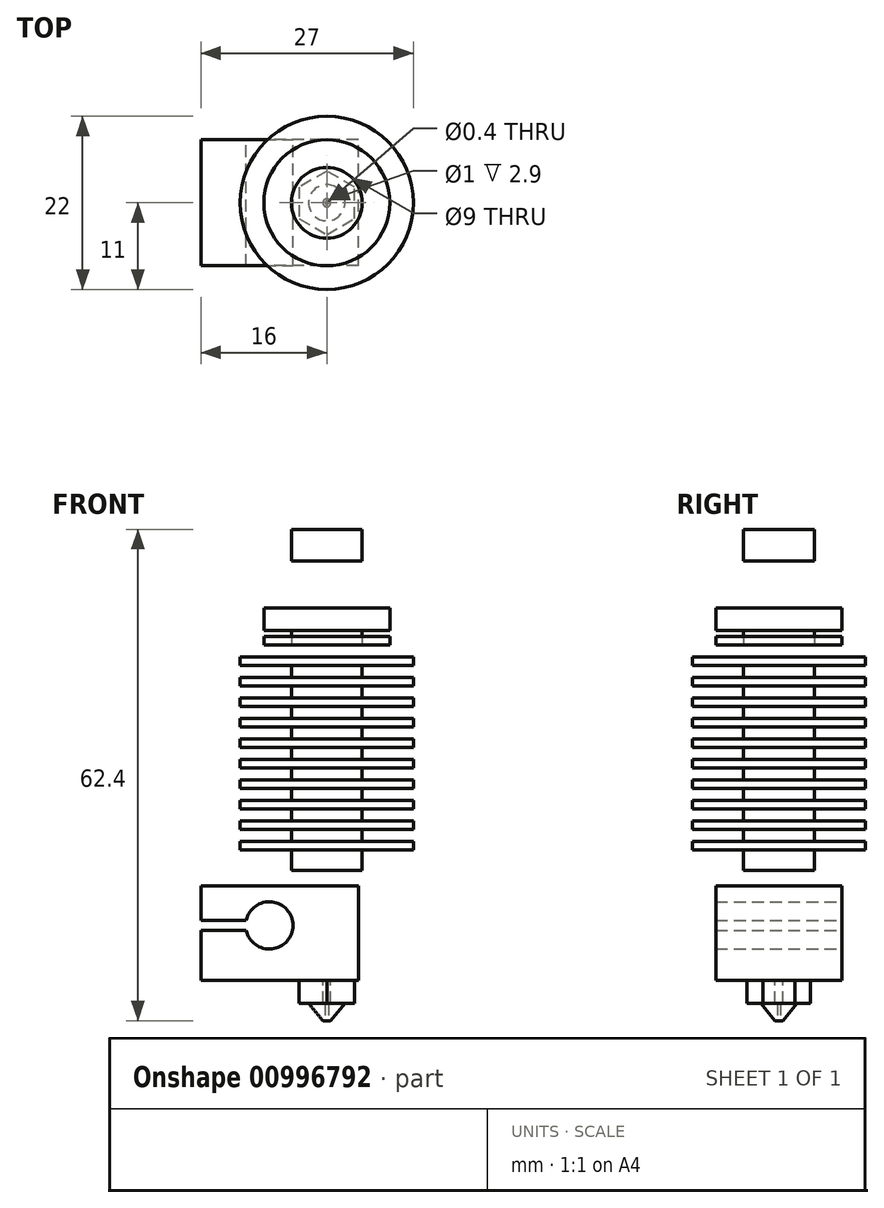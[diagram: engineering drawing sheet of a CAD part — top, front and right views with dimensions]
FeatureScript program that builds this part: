
annotation { "Feature Type Name" : "Feature", "Feature Type Description" : "" }
export const myFeature = defineFeature(function(context is Context, id is Id, definition is map)
    precondition{}
    {
        {
            var Q0;
            Q0=qCreatedBy(makeId("Front.planeOp"),FACE);
            var sketch = newSketch(context, id + "F0", { "sketchPlane" : qUnion([Q0])});
            skLineSegment(sketch, "E0.bottom", {"start": v(0, 0) * mm, "end": v(-11, 0) * mm});
            skLineSegment(sketch, "E0.top", {"start": v(0, 1.1) * mm, "end": v(-11, 1.1) * mm});
            skLineSegment(sketch, "E0.left", {"start": v(0, 0) * mm, "end": v(0, 1.1) * mm});
            skLineSegment(sketch, "E0.right", {"start": v(-11, 0) * mm, "end": v(-11, 1.1) * mm});
            skLineSegment(sketch, "E1.0.1.0", {"start": v(0, 3.7) * mm, "end": v(-11, 3.7) * mm});
            skLineSegment(sketch, "E1.0.1.1", {"start": v(-11, 2.6) * mm, "end": v(-11, 3.7) * mm});
            skLineSegment(sketch, "E1.0.1.2", {"start": v(0, 2.6) * mm, "end": v(-11, 2.6) * mm});
            skLineSegment(sketch, "E1.0.1.3", {"start": v(0, 2.6) * mm, "end": v(0, 3.7) * mm});
            skLineSegment(sketch, "E1.0.2.0", {"start": v(0, 6.3) * mm, "end": v(-11, 6.3) * mm});
            skLineSegment(sketch, "E1.0.2.1", {"start": v(-11, 5.2) * mm, "end": v(-11, 6.3) * mm});
            skLineSegment(sketch, "E1.0.2.2", {"start": v(0, 5.2) * mm, "end": v(-11, 5.2) * mm});
            skLineSegment(sketch, "E1.0.2.3", {"start": v(0, 5.2) * mm, "end": v(0, 6.3) * mm});
            skLineSegment(sketch, "E1.0.3.0", {"start": v(0, 8.9) * mm, "end": v(-11, 8.9) * mm});
            skLineSegment(sketch, "E1.0.3.1", {"start": v(-11, 7.8) * mm, "end": v(-11, 8.9) * mm});
            skLineSegment(sketch, "E1.0.3.2", {"start": v(0, 7.8) * mm, "end": v(-11, 7.8) * mm});
            skLineSegment(sketch, "E1.0.3.3", {"start": v(0, 7.8) * mm, "end": v(0, 8.9) * mm});
            skLineSegment(sketch, "E1.0.4.0", {"start": v(0, 11.5) * mm, "end": v(-11, 11.5) * mm});
            skLineSegment(sketch, "E1.0.4.1", {"start": v(-11, 10.4) * mm, "end": v(-11, 11.5) * mm});
            skLineSegment(sketch, "E1.0.4.2", {"start": v(0, 10.4) * mm, "end": v(-11, 10.4) * mm});
            skLineSegment(sketch, "E1.0.4.3", {"start": v(0, 10.4) * mm, "end": v(0, 11.5) * mm});
            skLineSegment(sketch, "E1.0.5.0", {"start": v(0, 14.1) * mm, "end": v(-11, 14.1) * mm});
            skLineSegment(sketch, "E1.0.5.1", {"start": v(-11, 13) * mm, "end": v(-11, 14.1) * mm});
            skLineSegment(sketch, "E1.0.5.2", {"start": v(0, 13) * mm, "end": v(-11, 13) * mm});
            skLineSegment(sketch, "E1.0.5.3", {"start": v(0, 13) * mm, "end": v(0, 14.1) * mm});
            skLineSegment(sketch, "E1.0.6.0", {"start": v(0, 16.7) * mm, "end": v(-11, 16.7) * mm});
            skLineSegment(sketch, "E1.0.6.1", {"start": v(-11, 15.6) * mm, "end": v(-11, 16.7) * mm});
            skLineSegment(sketch, "E1.0.6.2", {"start": v(0, 15.6) * mm, "end": v(-11, 15.6) * mm});
            skLineSegment(sketch, "E1.0.6.3", {"start": v(0, 15.6) * mm, "end": v(0, 16.7) * mm});
            skLineSegment(sketch, "E1.0.7.0", {"start": v(0, 19.3) * mm, "end": v(-11, 19.3) * mm});
            skLineSegment(sketch, "E1.0.7.1", {"start": v(-11, 18.2) * mm, "end": v(-11, 19.3) * mm});
            skLineSegment(sketch, "E1.0.7.2", {"start": v(0, 18.2) * mm, "end": v(-11, 18.2) * mm});
            skLineSegment(sketch, "E1.0.7.3", {"start": v(0, 18.2) * mm, "end": v(0, 19.3) * mm});
            skLineSegment(sketch, "E1.0.8.0", {"start": v(0, 21.9) * mm, "end": v(-11, 21.9) * mm});
            skLineSegment(sketch, "E1.0.8.1", {"start": v(-11, 20.8) * mm, "end": v(-11, 21.9) * mm});
            skLineSegment(sketch, "E1.0.8.2", {"start": v(0, 20.8) * mm, "end": v(-11, 20.8) * mm});
            skLineSegment(sketch, "E1.0.8.3", {"start": v(0, 20.8) * mm, "end": v(0, 21.9) * mm});
            skLineSegment(sketch, "E1.0.9.0", {"start": v(0, 24.5) * mm, "end": v(-11, 24.5) * mm});
            skLineSegment(sketch, "E1.0.9.1", {"start": v(-11, 23.4) * mm, "end": v(-11, 24.5) * mm});
            skLineSegment(sketch, "E1.0.9.2", {"start": v(0, 23.4) * mm, "end": v(-11, 23.4) * mm});
            skLineSegment(sketch, "E1.0.9.3", {"start": v(0, 23.4) * mm, "end": v(0, 24.5) * mm});
            skLineSegment(sketch, "E1.0.10.0", {"start": v(0, 27.1) * mm, "end": v(-11, 27.1) * mm});
            skLineSegment(sketch, "E1.0.10.1", {"start": v(-11, 26) * mm, "end": v(-11, 27.1) * mm});
            skLineSegment(sketch, "E1.0.10.2", {"start": v(0, 26) * mm, "end": v(-11, 26) * mm});
            skLineSegment(sketch, "E1.0.10.3", {"start": v(0, 26) * mm, "end": v(0, 27.1) * mm});
            skLineSegment(sketch, "E1.direction1", {"start": v(-11, 0) * mm, "end": v(14, 0) * mm, "construction": true});
            skLineSegment(sketch, "E1.direction2", {"start": v(-11, 0) * mm, "end": v(-11, 2.6) * mm, "construction": true});
            skLineSegment(sketch, "E2.bottom", {"start": v(0, 0) * mm, "end": v(-4.5, 0) * mm});
            skLineSegment(sketch, "E2.top", {"start": v(0, 30.5) * mm, "end": v(-4.5, 30.5) * mm});
            skLineSegment(sketch, "E2.left", {"start": v(0, 0) * mm, "end": v(0, 30.5) * mm});
            skLineSegment(sketch, "E2.right", {"start": v(-4.5, 0) * mm, "end": v(-4.5, 30.5) * mm});
            skLineSegment(sketch, "E3", {"start": v(0, 27.1) * mm, "end": v(0, 28.6) * mm});
            skLineSegment(sketch, "E4.bottom", {"start": v(0, 28.6) * mm, "end": v(-8, 28.6) * mm});
            skLineSegment(sketch, "E4.top", {"start": v(0, 29.7) * mm, "end": v(-8, 29.7) * mm});
            skLineSegment(sketch, "E4.left", {"start": v(0, 28.6) * mm, "end": v(0, 29.7) * mm});
            skLineSegment(sketch, "E4.right", {"start": v(-8, 28.6) * mm, "end": v(-8, 29.7) * mm});
            skLineSegment(sketch, "E5.bottom", {"start": v(0, 30.5) * mm, "end": v(-8, 30.5) * mm});
            skLineSegment(sketch, "E5.top", {"start": v(0, 33.3) * mm, "end": v(-8, 33.3) * mm});
            skLineSegment(sketch, "E5.left", {"start": v(0, 30.5) * mm, "end": v(0, 33.3) * mm});
            skLineSegment(sketch, "E5.right", {"start": v(-8, 30.5) * mm, "end": v(-8, 33.3) * mm});
            skLineSegment(sketch, "E6.bottom", {"start": v(0, 33.3) * mm, "end": v(-6, 33.3) * mm});
            skLineSegment(sketch, "E6.top", {"start": v(0, 39.3) * mm, "end": v(-6, 39.3) * mm});
            skLineSegment(sketch, "E6.left", {"start": v(0, 33.3) * mm, "end": v(0, 39.3) * mm});
            skLineSegment(sketch, "E6.right", {"start": v(-6, 33.3) * mm, "end": v(-6, 39.3) * mm});
            skLineSegment(sketch, "E7.bottom", {"start": v(0, 39.3) * mm, "end": v(-8, 39.3) * mm});
            skLineSegment(sketch, "E7.top", {"start": v(0, 43.3) * mm, "end": v(-8, 43.3) * mm});
            skLineSegment(sketch, "E7.left", {"start": v(0, 39.3) * mm, "end": v(0, 43.3) * mm});
            skLineSegment(sketch, "E7.right", {"start": v(-8, 39.3) * mm, "end": v(-8, 43.3) * mm});
            skLineSegment(sketch, "E8.bottom", {"start": v(0, 33.3) * mm, "end": v(-4.5, 33.3) * mm});
            skLineSegment(sketch, "E8.top", {"start": v(0, 43.3) * mm, "end": v(-4.5, 43.3) * mm});
            skLineSegment(sketch, "E8.left", {"start": v(0, 33.3) * mm, "end": v(0, 43.3) * mm});
            skLineSegment(sketch, "E8.right", {"start": v(-4.5, 33.3) * mm, "end": v(-4.5, 43.3) * mm});
            skLineSegment(sketch, "E9.bottom", {"start": v(0, 0) * mm, "end": v(-4.15, 0) * mm});
            skLineSegment(sketch, "E9.top", {"start": v(0, -16.9) * mm, "end": v(-4.15, -16.9) * mm});
            skLineSegment(sketch, "E9.left", {"start": v(0, 0) * mm, "end": v(0, -16.9) * mm});
            skLineSegment(sketch, "E9.right", {"start": v(-4.15, 0) * mm, "end": v(-4.15, -16.9) * mm});
            skLineSegment(sketch, "E10", {"start": v(0, 0) * mm, "end": v(0, -2) * mm});
            skLineSegment(sketch, "E11", {"start": v(0, -2) * mm, "end": v(4, -2) * mm});
            skLineSegment(sketch, "E12.bottom", {"start": v(4, -2) * mm, "end": v(-16, -2) * mm});
            skLineSegment(sketch, "E12.top", {"start": v(4, -14) * mm, "end": v(-16, -14) * mm});
            skLineSegment(sketch, "E12.left", {"start": v(4, -2) * mm, "end": v(4, -14) * mm});
            skLineSegment(sketch, "E12.right", {"start": v(-16, -2) * mm, "end": v(-16, -14) * mm});
            skLineSegment(sketch, "E13.bottom", {"start": v(0, -16.9) * mm, "end": v(-0.2, -16.9) * mm});
            skLineSegment(sketch, "E13.top", {"start": v(0, -19.1) * mm, "end": v(-0.2, -19.1) * mm});
            skLineSegment(sketch, "E13.left", {"start": v(0, -16.9) * mm, "end": v(0, -19.1) * mm});
            skLineSegment(sketch, "E13.right", {"start": v(-0.2, -16.9) * mm, "end": v(-0.2, -19.1) * mm});
            skLineSegment(sketch, "E14", {"start": v(-0.2, -19.1) * mm, "end": v(-0.5, -19.1) * mm});
            skLineSegment(sketch, "E15", {"start": v(-0.2, -16.9) * mm, "end": v(-2.3, -16.9) * mm});
            skLineSegment(sketch, "E16", {"start": v(-2.3, -16.9) * mm, "end": v(-0.5, -19.1) * mm});
            skLineSegment(sketch, "E17", {"start": v(4, -14) * mm, "end": v(4, -7) * mm});
            skLineSegment(sketch, "E18", {"start": v(4, -7) * mm, "end": v(-7.3, -7) * mm, "construction": true});
            skCircle(sketch, "E19", {"center": v(-7.3, -7) * mm, "radius": 3 * mm});
            skLineSegment(sketch, "E20", {"start": v(-7.3, -7) * mm, "end": v(-7.3, -6.35) * mm, "construction": true});
            skLineSegment(sketch, "E21", {"start": v(-7.3, -7) * mm, "end": v(-7.3, -7.65) * mm, "construction": true});
            skLineSegment(sketch, "E22", {"start": v(-7.3, -7.65) * mm, "end": v(-16, -7.65) * mm});
            skLineSegment(sketch, "E23", {"start": v(-7.3, -6.35) * mm, "end": v(-16, -6.35) * mm});
            skLineSegment(sketch, "E24", {"start": v(-2.3, -16.9) * mm, "end": v(-2.3, 0) * mm});
            skSolve(sketch);
        }
        {
            var Q0;
            Q0=makeQuery(id+"F0.imprint","IMPRINT",FACE,{"disambiguationData":[TD([[makeQuery(id+"F0.imprint","IMPRINT",EDGE,{"derivedFrom":sQuery(id+"F0.wireOp",EDGE,"E13.right")}),-1.0]])]});
            var Q1;
            {var subQ0=sQuery(id+"F0.wireOp",EDGE,"E13.bottom");Q1=makeQuery(id+"F0.imprint","IMPRINT",FACE,{"disambiguationData":[TD([[makeQuery(id+"F0.imprint","IMPRINT",EDGE,{"derivedFrom":subQ0}),-1.0]])]});}
            var Q2;
            {var subQ1=sQuery(id+"F0.wireOp",EDGE,"E2.bottom");Q2=makeQuery(id+"F0.imprint","IMPRINT",FACE,{"disambiguationData":[TD([[makeQuery(id+"F0.imprint","IMPRINT",EDGE,{"derivedFrom":subQ1}),-1.0]])]});}
            var Q3;
            {var subQ0=sQuery(id+"F0.wireOp",EDGE,"E0.bottom");Q3=makeQuery(id+"F0.imprint","IMPRINT",FACE,{"disambiguationData":[TD([[makeQuery(id+"F0.imprint","IMPRINT",EDGE,{"derivedFrom":subQ0}),-1.0]])]});}
            var Q4;
            {var subQ0=sQuery(id+"F0.wireOp",EDGE,"E2.left");var subQ1=sQuery(id+"F0.wireOp",EDGE,"E0.top");var subQ2=makeQuery(id+"F0.imprint","INTERSECT",VERTEX,{"derivedFrom":[subQ1,subQ0]});Q4=makeQuery(id+"F0.imprint","IMPRINT",FACE,{"disambiguationData":[TD([[makeQuery(id+"F0.imprint","IMPRINT",EDGE,{"disambiguationData":[TD([[subQ2,-1.0]])],"derivedFrom":subQ1}),-1.0]])]});}
            var Q5;
            {var subQ0=sQuery(id+"F0.wireOp",EDGE,"E2.left");var subQ1=sQuery(id+"F0.wireOp",EDGE,"E1.0.1.0");var subQ2=makeQuery(id+"F0.imprint","INTERSECT",VERTEX,{"derivedFrom":[subQ1,subQ0]});Q5=makeQuery(id+"F0.imprint","IMPRINT",FACE,{"disambiguationData":[TD([[makeQuery(id+"F0.imprint","IMPRINT",EDGE,{"disambiguationData":[TD([[subQ2,-1.0]])],"derivedFrom":subQ1}),1.0]])]});}
            var Q6;
            {var subQ0=sQuery(id+"F0.wireOp",EDGE,"E1.0.1.1");Q6=makeQuery(id+"F0.imprint","IMPRINT",FACE,{"disambiguationData":[TD([[makeQuery(id+"F0.imprint","IMPRINT",EDGE,{"derivedFrom":subQ0}),-1.0]])]});}
            var Q7;
            {var subQ0=sQuery(id+"F0.wireOp",EDGE,"E2.left");var subQ1=sQuery(id+"F0.wireOp",EDGE,"E1.0.1.0");var subQ2=makeQuery(id+"F0.imprint","INTERSECT",VERTEX,{"derivedFrom":[subQ1,subQ0]});Q7=makeQuery(id+"F0.imprint","IMPRINT",FACE,{"disambiguationData":[TD([[makeQuery(id+"F0.imprint","IMPRINT",EDGE,{"disambiguationData":[TD([[subQ2,-1.0]])],"derivedFrom":subQ1}),-1.0]])]});}
            var Q8;
            {var subQ0=sQuery(id+"F0.wireOp",EDGE,"E2.left");var subQ1=sQuery(id+"F0.wireOp",EDGE,"E1.0.2.0");var subQ2=makeQuery(id+"F0.imprint","INTERSECT",VERTEX,{"derivedFrom":[subQ1,subQ0]});Q8=makeQuery(id+"F0.imprint","IMPRINT",FACE,{"disambiguationData":[TD([[makeQuery(id+"F0.imprint","IMPRINT",EDGE,{"disambiguationData":[TD([[subQ2,-1.0]])],"derivedFrom":subQ1}),1.0]])]});}
            var Q9;
            {var subQ0=sQuery(id+"F0.wireOp",EDGE,"E2.left");var subQ1=sQuery(id+"F0.wireOp",EDGE,"E1.0.2.0");var subQ2=makeQuery(id+"F0.imprint","INTERSECT",VERTEX,{"derivedFrom":[subQ1,subQ0]});Q9=makeQuery(id+"F0.imprint","IMPRINT",FACE,{"disambiguationData":[TD([[makeQuery(id+"F0.imprint","IMPRINT",EDGE,{"disambiguationData":[TD([[subQ2,-1.0]])],"derivedFrom":subQ1}),-1.0]])]});}
            var Q10;
            {var subQ0=sQuery(id+"F0.wireOp",EDGE,"E2.left");var subQ1=sQuery(id+"F0.wireOp",EDGE,"E1.0.3.0");var subQ2=makeQuery(id+"F0.imprint","INTERSECT",VERTEX,{"derivedFrom":[subQ1,subQ0]});Q10=makeQuery(id+"F0.imprint","IMPRINT",FACE,{"disambiguationData":[TD([[makeQuery(id+"F0.imprint","IMPRINT",EDGE,{"disambiguationData":[TD([[subQ2,-1.0]])],"derivedFrom":subQ1}),1.0]])]});}
            var Q11;
            {var subQ0=sQuery(id+"F0.wireOp",EDGE,"E1.0.2.1");Q11=makeQuery(id+"F0.imprint","IMPRINT",FACE,{"disambiguationData":[TD([[makeQuery(id+"F0.imprint","IMPRINT",EDGE,{"derivedFrom":subQ0}),-1.0]])]});}
            var Q12;
            {var subQ0=sQuery(id+"F0.wireOp",EDGE,"E1.0.3.1");Q12=makeQuery(id+"F0.imprint","IMPRINT",FACE,{"disambiguationData":[TD([[makeQuery(id+"F0.imprint","IMPRINT",EDGE,{"derivedFrom":subQ0}),-1.0]])]});}
            var Q13;
            {var subQ0=sQuery(id+"F0.wireOp",EDGE,"E2.left");var subQ1=sQuery(id+"F0.wireOp",EDGE,"E1.0.3.0");var subQ2=makeQuery(id+"F0.imprint","INTERSECT",VERTEX,{"derivedFrom":[subQ1,subQ0]});Q13=makeQuery(id+"F0.imprint","IMPRINT",FACE,{"disambiguationData":[TD([[makeQuery(id+"F0.imprint","IMPRINT",EDGE,{"disambiguationData":[TD([[subQ2,-1.0]])],"derivedFrom":subQ1}),-1.0]])]});}
            var Q14;
            {var subQ0=sQuery(id+"F0.wireOp",EDGE,"E2.left");var subQ1=sQuery(id+"F0.wireOp",EDGE,"E1.0.4.0");var subQ2=makeQuery(id+"F0.imprint","INTERSECT",VERTEX,{"derivedFrom":[subQ1,subQ0]});Q14=makeQuery(id+"F0.imprint","IMPRINT",FACE,{"disambiguationData":[TD([[makeQuery(id+"F0.imprint","IMPRINT",EDGE,{"disambiguationData":[TD([[subQ2,-1.0]])],"derivedFrom":subQ1}),1.0]])]});}
            var Q15;
            {var subQ0=sQuery(id+"F0.wireOp",EDGE,"E1.0.4.1");Q15=makeQuery(id+"F0.imprint","IMPRINT",FACE,{"disambiguationData":[TD([[makeQuery(id+"F0.imprint","IMPRINT",EDGE,{"derivedFrom":subQ0}),-1.0]])]});}
            var Q16;
            {var subQ0=sQuery(id+"F0.wireOp",EDGE,"E2.left");var subQ1=sQuery(id+"F0.wireOp",EDGE,"E1.0.4.0");var subQ2=makeQuery(id+"F0.imprint","INTERSECT",VERTEX,{"derivedFrom":[subQ1,subQ0]});Q16=makeQuery(id+"F0.imprint","IMPRINT",FACE,{"disambiguationData":[TD([[makeQuery(id+"F0.imprint","IMPRINT",EDGE,{"disambiguationData":[TD([[subQ2,-1.0]])],"derivedFrom":subQ1}),-1.0]])]});}
            var Q17;
            {var subQ0=sQuery(id+"F0.wireOp",EDGE,"E2.left");var subQ1=sQuery(id+"F0.wireOp",EDGE,"E1.0.5.0");var subQ2=makeQuery(id+"F0.imprint","INTERSECT",VERTEX,{"derivedFrom":[subQ1,subQ0]});Q17=makeQuery(id+"F0.imprint","IMPRINT",FACE,{"disambiguationData":[TD([[makeQuery(id+"F0.imprint","IMPRINT",EDGE,{"disambiguationData":[TD([[subQ2,-1.0]])],"derivedFrom":subQ1}),1.0]])]});}
            var Q18;
            {var subQ0=sQuery(id+"F0.wireOp",EDGE,"E2.left");var subQ1=sQuery(id+"F0.wireOp",EDGE,"E1.0.5.0");var subQ2=makeQuery(id+"F0.imprint","INTERSECT",VERTEX,{"derivedFrom":[subQ1,subQ0]});Q18=makeQuery(id+"F0.imprint","IMPRINT",FACE,{"disambiguationData":[TD([[makeQuery(id+"F0.imprint","IMPRINT",EDGE,{"disambiguationData":[TD([[subQ2,-1.0]])],"derivedFrom":subQ1}),-1.0]])]});}
            var Q19;
            {var subQ0=sQuery(id+"F0.wireOp",EDGE,"E2.left");var subQ1=sQuery(id+"F0.wireOp",EDGE,"E1.0.6.0");var subQ2=makeQuery(id+"F0.imprint","INTERSECT",VERTEX,{"derivedFrom":[subQ1,subQ0]});Q19=makeQuery(id+"F0.imprint","IMPRINT",FACE,{"disambiguationData":[TD([[makeQuery(id+"F0.imprint","IMPRINT",EDGE,{"disambiguationData":[TD([[subQ2,-1.0]])],"derivedFrom":subQ1}),1.0]])]});}
            var Q20;
            {var subQ0=sQuery(id+"F0.wireOp",EDGE,"E2.left");var subQ1=sQuery(id+"F0.wireOp",EDGE,"E1.0.6.0");var subQ2=makeQuery(id+"F0.imprint","INTERSECT",VERTEX,{"derivedFrom":[subQ1,subQ0]});Q20=makeQuery(id+"F0.imprint","IMPRINT",FACE,{"disambiguationData":[TD([[makeQuery(id+"F0.imprint","IMPRINT",EDGE,{"disambiguationData":[TD([[subQ2,-1.0]])],"derivedFrom":subQ1}),-1.0]])]});}
            var Q21;
            {var subQ0=sQuery(id+"F0.wireOp",EDGE,"E2.left");var subQ1=sQuery(id+"F0.wireOp",EDGE,"E1.0.7.0");var subQ2=makeQuery(id+"F0.imprint","INTERSECT",VERTEX,{"derivedFrom":[subQ1,subQ0]});Q21=makeQuery(id+"F0.imprint","IMPRINT",FACE,{"disambiguationData":[TD([[makeQuery(id+"F0.imprint","IMPRINT",EDGE,{"disambiguationData":[TD([[subQ2,-1.0]])],"derivedFrom":subQ1}),1.0]])]});}
            var Q22;
            {var subQ0=sQuery(id+"F0.wireOp",EDGE,"E2.left");var subQ1=sQuery(id+"F0.wireOp",EDGE,"E1.0.7.0");var subQ2=makeQuery(id+"F0.imprint","INTERSECT",VERTEX,{"derivedFrom":[subQ1,subQ0]});Q22=makeQuery(id+"F0.imprint","IMPRINT",FACE,{"disambiguationData":[TD([[makeQuery(id+"F0.imprint","IMPRINT",EDGE,{"disambiguationData":[TD([[subQ2,-1.0]])],"derivedFrom":subQ1}),-1.0]])]});}
            var Q23;
            {var subQ0=sQuery(id+"F0.wireOp",EDGE,"E2.left");var subQ1=sQuery(id+"F0.wireOp",EDGE,"E1.0.8.0");var subQ2=makeQuery(id+"F0.imprint","INTERSECT",VERTEX,{"derivedFrom":[subQ1,subQ0]});Q23=makeQuery(id+"F0.imprint","IMPRINT",FACE,{"disambiguationData":[TD([[makeQuery(id+"F0.imprint","IMPRINT",EDGE,{"disambiguationData":[TD([[subQ2,-1.0]])],"derivedFrom":subQ1}),1.0]])]});}
            var Q24;
            {var subQ0=sQuery(id+"F0.wireOp",EDGE,"E2.left");var subQ1=sQuery(id+"F0.wireOp",EDGE,"E1.0.8.0");var subQ2=makeQuery(id+"F0.imprint","INTERSECT",VERTEX,{"derivedFrom":[subQ1,subQ0]});Q24=makeQuery(id+"F0.imprint","IMPRINT",FACE,{"disambiguationData":[TD([[makeQuery(id+"F0.imprint","IMPRINT",EDGE,{"disambiguationData":[TD([[subQ2,-1.0]])],"derivedFrom":subQ1}),-1.0]])]});}
            var Q25;
            {var subQ0=sQuery(id+"F0.wireOp",EDGE,"E2.left");var subQ1=sQuery(id+"F0.wireOp",EDGE,"E1.0.9.0");var subQ2=makeQuery(id+"F0.imprint","INTERSECT",VERTEX,{"derivedFrom":[subQ1,subQ0]});Q25=makeQuery(id+"F0.imprint","IMPRINT",FACE,{"disambiguationData":[TD([[makeQuery(id+"F0.imprint","IMPRINT",EDGE,{"disambiguationData":[TD([[subQ2,-1.0]])],"derivedFrom":subQ1}),1.0]])]});}
            var Q26;
            {var subQ0=sQuery(id+"F0.wireOp",EDGE,"E2.left");var subQ1=sQuery(id+"F0.wireOp",EDGE,"E1.0.9.0");var subQ2=makeQuery(id+"F0.imprint","INTERSECT",VERTEX,{"derivedFrom":[subQ1,subQ0]});Q26=makeQuery(id+"F0.imprint","IMPRINT",FACE,{"disambiguationData":[TD([[makeQuery(id+"F0.imprint","IMPRINT",EDGE,{"disambiguationData":[TD([[subQ2,-1.0]])],"derivedFrom":subQ1}),-1.0]])]});}
            var Q27;
            {var subQ0=sQuery(id+"F0.wireOp",EDGE,"E2.left");var subQ5=sQuery(id+"F0.wireOp",EDGE,"E1.0.10.2");var subQ6=makeQuery(id+"F0.imprint","INTERSECT",VERTEX,{"derivedFrom":[subQ5,subQ0]});Q27=makeQuery(id+"F0.imprint","IMPRINT",FACE,{"disambiguationData":[TD([[makeQuery(id+"F0.imprint","IMPRINT",EDGE,{"disambiguationData":[TD([[subQ6,-1.0]])],"derivedFrom":subQ5}),-1.0]])]});}
            var Q28;
            {var subQ0=sQuery(id+"F0.wireOp",EDGE,"E1.0.10.1");Q28=makeQuery(id+"F0.imprint","IMPRINT",FACE,{"disambiguationData":[TD([[makeQuery(id+"F0.imprint","IMPRINT",EDGE,{"derivedFrom":subQ0}),-1.0]])]});}
            var Q29;
            {var subQ0=sQuery(id+"F0.wireOp",EDGE,"E1.0.9.1");Q29=makeQuery(id+"F0.imprint","IMPRINT",FACE,{"disambiguationData":[TD([[makeQuery(id+"F0.imprint","IMPRINT",EDGE,{"derivedFrom":subQ0}),-1.0]])]});}
            var Q30;
            {var subQ0=sQuery(id+"F0.wireOp",EDGE,"E1.0.8.1");Q30=makeQuery(id+"F0.imprint","IMPRINT",FACE,{"disambiguationData":[TD([[makeQuery(id+"F0.imprint","IMPRINT",EDGE,{"derivedFrom":subQ0}),-1.0]])]});}
            var Q31;
            {var subQ0=sQuery(id+"F0.wireOp",EDGE,"E1.0.7.1");Q31=makeQuery(id+"F0.imprint","IMPRINT",FACE,{"disambiguationData":[TD([[makeQuery(id+"F0.imprint","IMPRINT",EDGE,{"derivedFrom":subQ0}),-1.0]])]});}
            var Q32;
            {var subQ0=sQuery(id+"F0.wireOp",EDGE,"E1.0.6.1");Q32=makeQuery(id+"F0.imprint","IMPRINT",FACE,{"disambiguationData":[TD([[makeQuery(id+"F0.imprint","IMPRINT",EDGE,{"derivedFrom":subQ0}),-1.0]])]});}
            var Q33;
            {var subQ0=sQuery(id+"F0.wireOp",EDGE,"E1.0.5.1");Q33=makeQuery(id+"F0.imprint","IMPRINT",FACE,{"disambiguationData":[TD([[makeQuery(id+"F0.imprint","IMPRINT",EDGE,{"derivedFrom":subQ0}),-1.0]])]});}
            var Q34;
            {var subQ5=sQuery(id+"F0.wireOp",EDGE,"E4.left");Q34=makeQuery(id+"F0.imprint","IMPRINT",FACE,{"disambiguationData":[TD([[makeQuery(id+"F0.imprint","IMPRINT",EDGE,{"derivedFrom":subQ5}),1.0]])]});}
            var Q35;
            {var subQ0=sQuery(id+"F0.wireOp",EDGE,"E3");Q35=makeQuery(id+"F0.imprint","IMPRINT",FACE,{"disambiguationData":[TD([[makeQuery(id+"F0.imprint","IMPRINT",EDGE,{"derivedFrom":subQ0}),1.0]])]});}
            var Q36;
            {var subQ5=sQuery(id+"F0.wireOp",EDGE,"E4.right");Q36=makeQuery(id+"F0.imprint","IMPRINT",FACE,{"disambiguationData":[TD([[makeQuery(id+"F0.imprint","IMPRINT",EDGE,{"derivedFrom":subQ5}),-1.0]])]});}
            var Q37;
            {var subQ0=sQuery(id+"F0.wireOp",EDGE,"E5.bottom");var subQ5=sQuery(id+"F0.wireOp",EDGE,"E2.right");var subQ6=makeQuery(id+"F0.imprint","INTERSECT",VERTEX,{"derivedFrom":[subQ5,subQ0]});Q37=makeQuery(id+"F0.imprint","IMPRINT",FACE,{"disambiguationData":[TD([[makeQuery(id+"F0.imprint","IMPRINT",EDGE,{"disambiguationData":[TD([[subQ6,1.0]])],"derivedFrom":subQ5}),-1.0]])]});}
            var Q38;
            Q38=makeQuery(id+"F0.imprint","IMPRINT",FACE,{"disambiguationData":[TD([[makeQuery(id+"F0.imprint","IMPRINT",EDGE,{"derivedFrom":sQuery(id+"F0.wireOp",EDGE,"E5.top")}),1.0]])]});
            var Q39;
            {var subQ0=sQuery(id+"F0.wireOp",EDGE,"E6.bottom");Q39=makeQuery(id+"F0.imprint","IMPRINT",FACE,{"disambiguationData":[TD([[makeQuery(id+"F0.imprint","IMPRINT",EDGE,{"derivedFrom":subQ0}),-1.0]])]});}
            var Q40;
            {var subQ1=sQuery(id+"F0.wireOp",EDGE,"E7.top");Q40=makeQuery(id+"F0.imprint","IMPRINT",FACE,{"disambiguationData":[TD([[makeQuery(id+"F0.imprint","IMPRINT",EDGE,{"derivedFrom":subQ1}),1.0]])]});}
            var Q41;
            {var subQ0=sQuery(id+"F0.wireOp",EDGE,"E10");Q41=makeQuery(id+"F0.imprint","IMPRINT",FACE,{"disambiguationData":[TD([[makeQuery(id+"F0.imprint","IMPRINT",EDGE,{"derivedFrom":subQ0}),-1.0]])]});}
            var Q42;
            {var subQ1=sQuery(id+"F0.wireOp",EDGE,"E9.left");var subQ3=sQuery(id+"F0.wireOp",EDGE,"E12.top");var subQ4=makeQuery(id+"F0.imprint","INTERSECT",VERTEX,{"derivedFrom":[subQ1,subQ3]});Q42=makeQuery(id+"F0.imprint","IMPRINT",FACE,{"disambiguationData":[TD([[makeQuery(id+"F0.imprint","IMPRINT",EDGE,{"disambiguationData":[TD([[subQ4,-1.0]])],"derivedFrom":subQ3}),-1.0]])]});}
            var Q43;
            Q43=sQuery(id+"F0.wireOp",EDGE,"E6.left");
            revolve(context, id + "F1", {"surfaceOperationType" : NewSurfaceOperationType.NEW, "entities" : qUnion([Q0, Q1, Q2, Q3, Q4, Q5, Q6, Q7, Q8, Q9, Q10, Q11, Q12, Q13, Q14, Q15, Q16, Q17, Q18, Q19, Q20, Q21, Q22, Q23, Q24, Q25, Q26, Q27, Q28, Q29, Q30, Q31, Q32, Q33, Q34, Q35, Q36, Q37, Q38, Q39, Q40, Q41, Q42]), "axis" : qUnion([Q43]), "revolveType" : RevolveType.FULL});
        }
        {
            var Q0;
            {var subQ1=sQuery(id+"F0.wireOp",EDGE,"E12.bottom");var subQ5=sQuery(id+"F0.wireOp",EDGE,"E9.right");var subQ6=makeQuery(id+"F0.imprint","INTERSECT",VERTEX,{"derivedFrom":[subQ5,subQ1]});Q0=makeQuery(id+"F0.imprint","IMPRINT",FACE,{"disambiguationData":[TD([[makeQuery(id+"F0.imprint","IMPRINT",EDGE,{"disambiguationData":[TD([[subQ6,-1.0]])],"derivedFrom":subQ5}),-1.0]])]});}
            var Q1;
            {var subQ0=sQuery(id+"F0.wireOp",EDGE,"E12.bottom");var subQ3=sQuery(id+"F0.wireOp",EDGE,"E9.right");var subQ4=makeQuery(id+"F0.imprint","INTERSECT",VERTEX,{"derivedFrom":[subQ3,subQ0]});Q1=makeQuery(id+"F0.imprint","IMPRINT",FACE,{"disambiguationData":[TD([[makeQuery(id+"F0.imprint","IMPRINT",EDGE,{"disambiguationData":[TD([[subQ4,-1.0]])],"derivedFrom":subQ3}),1.0]])]});}
            var Q2;
            {var subQ0=sQuery(id+"F0.wireOp",EDGE,"E12.left");Q2=makeQuery(id+"F0.imprint","IMPRINT",FACE,{"disambiguationData":[TD([[makeQuery(id+"F0.imprint","IMPRINT",EDGE,{"derivedFrom":subQ0}),-1.0]])]});}
            var Q3;
            {var subQ1=sQuery(id+"F0.wireOp",EDGE,"E9.left");var subQ3=sQuery(id+"F0.wireOp",EDGE,"E12.top");var subQ4=makeQuery(id+"F0.imprint","INTERSECT",VERTEX,{"derivedFrom":[subQ1,subQ3]});Q3=makeQuery(id+"F0.imprint","IMPRINT",FACE,{"disambiguationData":[TD([[makeQuery(id+"F0.imprint","IMPRINT",EDGE,{"disambiguationData":[TD([[subQ4,-1.0]])],"derivedFrom":subQ3}),-1.0]])]});}
            extrude(context, id + "F2", {"entities" : qUnion([Q0, Q1, Q2, Q3]), "operationType" : NewBodyOperationType.ADD, "endBound" : BoundingType.SYMMETRIC, "depth" : 16 * mm, "offsetDistance" : 25 * mm});
        }
        {
            var Q0;
            Q0=makeQuery(id+"F2.opExtrude","SWEPT_FACE",FACE,{"disambiguationData":[OSD([sQuery(id+"F0.wireOp",EDGE,"E12.bottom")])]});
            var sketch = newSketch(context, id + "F3", { "sketchPlane" : qUnion([Q0])});
            skLineSegment(sketch, "E25", {"start": v(0, 0) * mm, "end": v(4, 0) * mm});
            skLineSegment(sketch, "E26", {"start": v(4, 0) * mm, "end": v(4, 8) * mm});
            skLineSegment(sketch, "E27.bottom", {"start": v(4, 8) * mm, "end": v(-16, 8) * mm});
            skLineSegment(sketch, "E27.top", {"start": v(4, -8) * mm, "end": v(-16, -8) * mm});
            skLineSegment(sketch, "E27.left", {"start": v(4, 8) * mm, "end": v(4, -8) * mm});
            skLineSegment(sketch, "E27.right", {"start": v(-16, 8) * mm, "end": v(-16, -8) * mm});
            skLineSegment(sketch, "E28", {"start": v(0, 0) * mm, "end": v(-3.5, 0) * mm});
            skCircle(sketch, "E29.cCircle", {"center": v(0, 0) * mm, "radius": 3.5 * mm, "construction": true});
            skLineSegment(sketch, "E29.0", {"start": v(-3.5, -2.02) * mm, "end": v(-3.5, 2.02) * mm});
            skLineSegment(sketch, "E29.1", {"start": v(-3.5, 2.02) * mm, "end": v(0, 4.04) * mm});
            skLineSegment(sketch, "E29.2", {"start": v(0, 4.04) * mm, "end": v(3.5, 2.02) * mm});
            skLineSegment(sketch, "E29.3", {"start": v(3.5, 2.02) * mm, "end": v(3.5, -2.02) * mm});
            skLineSegment(sketch, "E29.4", {"start": v(3.5, -2.02) * mm, "end": v(0, -4.04) * mm});
            skLineSegment(sketch, "E29.5", {"start": v(0, -4.04) * mm, "end": v(-3.5, -2.02) * mm});
            skPoint(sketch, "E29.0.midPoint", {"position": v(-3.5, 0) * mm});
            skCircle(sketch, "E30", {"center": v(0, 0) * mm, "radius": 2 * mm});
            skCircle(sketch, "E31", {"center": v(0, 0) * mm, "radius": 0.5 * mm});
            skCircle(sketch, "E32", {"center": v(0, 0) * mm, "radius": 0.2 * mm});
            skSolve(sketch);
        }
        {
            var Q0;
            {var subQ0=sQuery(id+"F3.wireOp",EDGE,"E29.1");Q0=makeQuery(id+"F3.imprint","IMPRINT",FACE,{"disambiguationData":[TD([[makeQuery(id+"F3.imprint","IMPRINT",EDGE,{"derivedFrom":subQ0}),-1.0]])]});}
            var Q1;
            {var subQ0=sQuery(id+"F3.wireOp",EDGE,"E29.4");Q1=makeQuery(id+"F3.imprint","IMPRINT",FACE,{"disambiguationData":[TD([[makeQuery(id+"F3.imprint","IMPRINT",EDGE,{"derivedFrom":subQ0}),-1.0]])]});}
            var Q2;
            {var subQ0=sQuery(id+"F3.wireOp",EDGE,"E30");var subQ1=sQuery(id+"F3.wireOp",EDGE,"E25");var subQ2=makeQuery(id+"F3.imprint","INTERSECT",VERTEX,{"derivedFrom":[subQ1,subQ0]});Q2=makeQuery(id+"F3.imprint","IMPRINT",FACE,{"disambiguationData":[TD([[makeQuery(id+"F3.imprint","IMPRINT",EDGE,{"disambiguationData":[TD([[subQ2,1.0]])],"derivedFrom":subQ1}),-1.0]])]});}
            var Q3;
            {var subQ0=sQuery(id+"F3.wireOp",EDGE,"E30");var subQ1=sQuery(id+"F3.wireOp",EDGE,"E25");var subQ2=makeQuery(id+"F3.imprint","INTERSECT",VERTEX,{"derivedFrom":[subQ1,subQ0]});Q3=makeQuery(id+"F3.imprint","IMPRINT",FACE,{"disambiguationData":[TD([[makeQuery(id+"F3.imprint","IMPRINT",EDGE,{"disambiguationData":[TD([[subQ2,1.0]])],"derivedFrom":subQ1}),1.0]])]});}
            extrude(context, id + "F4", {"entities" : qUnion([Q0, Q1, Q2, Q3]), "operationType" : NewBodyOperationType.ADD, "oppositeDirection" : true, "depth" : 14.9 * mm, "offsetDistance" : 25 * mm});
        }
    });
